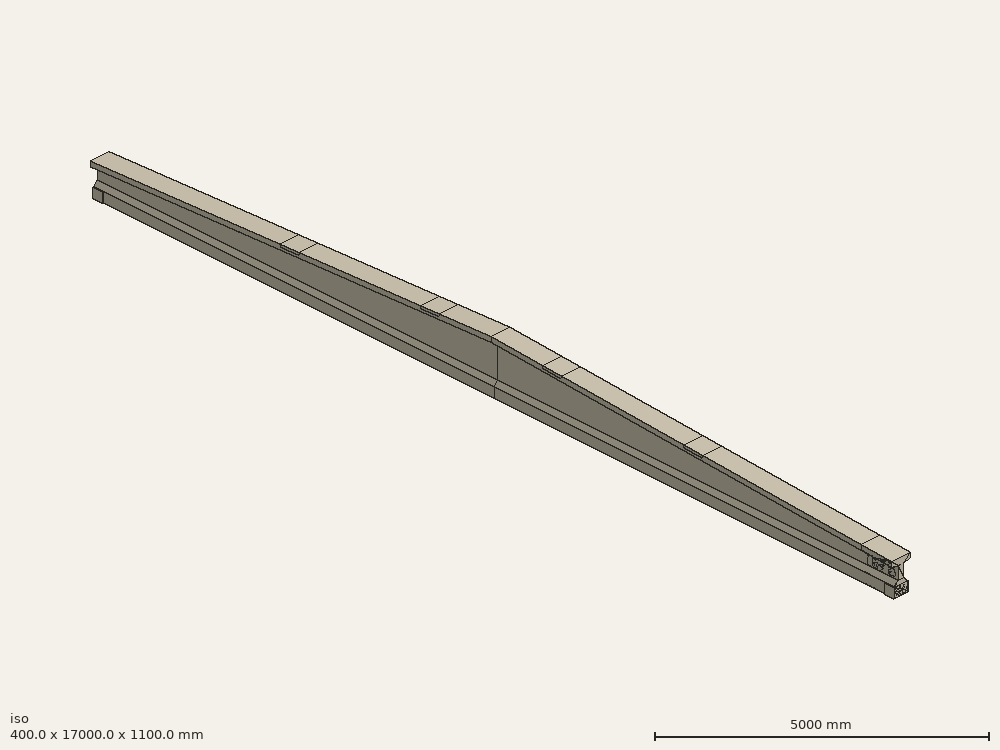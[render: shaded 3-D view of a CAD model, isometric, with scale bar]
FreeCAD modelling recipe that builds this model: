
FCSTD DOCUMENT  (FreeCAD 0.21R33694 (Git))
Label: beam_test
License: All rights reserved
LicenseURL: http://en.wikipedia.org/wiki/All_rights_reserved
objects: Fem::ConstraintForce×7, Sketcher::SketchObject×6, Part::FeaturePython×6, Part::Extrusion×3, Part::Feature×2, Fem::ConstraintDisplacement×2, Part::Loft×1, Part::Part2DObjectPython×1, App::DocumentObjectGroup×1, Part::Compound×1, Fem::FemSolverObjectPython×1, App::MaterialObjectPython×1, Fem::FeaturePython×1, Fem::FemMeshObjectPython×1, Fem::FemAnalysis×1
note: 20 computed .brp shape members not serialized (recipe doc carries the construction recipe); baked Part::Feature solids carry a one-line shape summary decoded from their .brp

FEATURE [Sketcher::SketchObject] Sketch
  FullyConstrained = true
  Placement = pos=(0,0,0) rot=(1,0,0;1.5708rad)
  sketch-geometry (12):
    g0: LineSegment StartX=-130 StartY=0 StartZ=0 EndX=130 EndY=4e-16 EndZ=0
    g1: LineSegment StartX=130 StartY=4e-16 StartZ=0 EndX=130 EndY=200 EndZ=0
    g2: LineSegment StartX=130 StartY=200 StartZ=0 EndX=60 EndY=290 EndZ=0
    g3: LineSegment StartX=60 StartY=290 StartZ=0 EndX=60 EndY=540 EndZ=0
    g4: LineSegment StartX=60 StartY=540 StartZ=0 EndX=200 EndY=570 EndZ=0
    g5: LineSegment StartX=200 StartY=570 StartZ=0 EndX=200 EndY=670 EndZ=0
    g6: LineSegment StartX=200 StartY=670 StartZ=0 EndX=-200 EndY=670 EndZ=0
    g7: LineSegment StartX=-200 StartY=670 StartZ=0 EndX=-200 EndY=570 EndZ=0
    g8: LineSegment StartX=-200 StartY=570 StartZ=0 EndX=-60 EndY=540 EndZ=0
    g9: LineSegment StartX=-60 StartY=540 StartZ=0 EndX=-60 EndY=290 EndZ=0
    g10: LineSegment StartX=-60 StartY=290 StartZ=0 EndX=-130 EndY=200 EndZ=0
    g11: LineSegment StartX=-130 StartY=200 StartZ=0 EndX=-130 EndY=0 EndZ=0
  constraints (33):
    c: PointOnObject(g0,g-1)
    c: Symmetric(g0,g0,g-2)
    c: DistanceX(g0,g0) = 260
    c: Coincident(g0,g1)
    c: Vertical(g1)
    c: Coincident(g1,g2)
    c: Coincident(g2,g3)
    c: Vertical(g3)
    c: Coincident(g3,g4)
    c: Coincident(g4,g5)
    c: Vertical(g5)
    c: Coincident(g5,g6)
    c: Coincident(g6,g7)
    c: Vertical(g7)
    c: Coincident(g7,g8)
    c: Coincident(g8,g9)
    c: Vertical(g9)
    c: Coincident(g9,g10)
    c: Coincident(g10,g11)
    c: Coincident(g11,g0)
    c: Vertical(g11)
    c: Equal(g11,g1)
    c: Symmetric(g9,g2,g-2)
    c: Equal(g9,g3)
    c: Symmetric(g6,g5,g-2)
    c: DistanceX(g6,g6) = 400
    c: DistanceY(g0,g5) = 670
    c: Equal(g7,g5)
    c: DistanceX(g9,g2) = 120
    c: DistanceY(g5,g5) = 100
    c: DistanceY(g3,g4) = 30
    c: DistanceY(g1,g1) = 200
    c: DistanceY(g1,g2) = 90
FEATURE [Sketcher::SketchObject] Sketch001
  FullyConstrained = true
  Placement = pos=(0,8500,0) rot=(1,0,0;1.5708rad)
  sketch-geometry (12):
    g0: LineSegment StartX=-130 StartY=0 StartZ=0 EndX=130 EndY=0 EndZ=0
    g1: LineSegment StartX=130 StartY=0 StartZ=0 EndX=130 EndY=200 EndZ=0
    g2: LineSegment StartX=130 StartY=200 StartZ=0 EndX=60 EndY=290 EndZ=0
    g3: LineSegment StartX=60 StartY=290 StartZ=0 EndX=60 EndY=970 EndZ=0
    g4: LineSegment StartX=60 StartY=970 StartZ=0 EndX=200 EndY=1000 EndZ=0
    g5: LineSegment StartX=200 StartY=1000 StartZ=0 EndX=200 EndY=1100 EndZ=0
    g6: LineSegment StartX=200 StartY=1100 StartZ=0 EndX=-200 EndY=1100 EndZ=0
    g7: LineSegment StartX=-200 StartY=1100 StartZ=0 EndX=-200 EndY=1000 EndZ=0
    g8: LineSegment StartX=-200 StartY=1000 StartZ=0 EndX=-60 EndY=970 EndZ=0
    g9: LineSegment StartX=-60 StartY=970 StartZ=0 EndX=-60 EndY=290 EndZ=0
    g10: LineSegment StartX=-60 StartY=290 StartZ=0 EndX=-130 EndY=200 EndZ=0
    g11: LineSegment StartX=-130 StartY=200 StartZ=0 EndX=-130 EndY=0 EndZ=0
  constraints (33):
    c: PointOnObject(g0,g-1)
    c: Symmetric(g0,g0,g-2)
    c: DistanceX(g0,g0) = 260
    c: Coincident(g0,g1)
    c: Vertical(g1)
    c: Coincident(g1,g2)
    c: Coincident(g2,g3)
    c: Vertical(g3)
    c: Coincident(g3,g4)
    c: Coincident(g4,g5)
    c: Vertical(g5)
    c: Coincident(g5,g6)
    c: Coincident(g6,g7)
    c: Vertical(g7)
    c: Coincident(g7,g8)
    c: Coincident(g8,g9)
    c: Vertical(g9)
    c: Coincident(g9,g10)
    c: Coincident(g10,g11)
    c: Coincident(g11,g0)
    c: Vertical(g11)
    c: Equal(g11,g1)
    c: Symmetric(g9,g2,g-2)
    c: Equal(g9,g3)
    c: Symmetric(g6,g5,g-2)
    c: DistanceX(g6,g6) = 400
    c: DistanceY(g0,g5) = 1100
    c: Equal(g7,g5)
    c: DistanceX(g9,g2) = 120
    c: DistanceY(g5,g5) = 100
    c: DistanceY(g3,g4) = 30
    c: DistanceY(g1,g1) = 200
    c: DistanceY(g1,g2) = 90
FEATURE [Part::Loft] Loft
  Closed = false
  MaxDegree = 5
  Ruled = false
  Sections = -> [Sketch,Sketch001]
  Solid = true
FEATURE [Part::Part2DObjectPython] Rectangle  # Draft 2D object (typed FeaturePython)
  Area = 3.16759e+06
  ChamferSize = 0
  Columns = 1
  FilletRadius = 0
  Height = 1690
  Length = 1874.31
  MakeFace = true
  Placement = pos=(-1011.48,650,-530.33) rot=(1,0,0;1.5708rad)
  Rows = 1
FEATURE [Part::Feature] Loft001
  Placement = pos=(1.041e-12,17000,0) rot=(0,0,1;3.14159rad)
  shape: bbox 400 x 8500 x 1100 mm, 14 faces (baked)
FEATURE [Part::Feature] Loft002
  shape: bbox 400 x 8500 x 1100 mm, 14 faces (baked)
FEATURE [Part::FeaturePython] Slice  # WARN: FeaturePython — macro-defined, semantics opaque (R4)
  Base = -> Loft002
  Mode = 1
  Tolerance = 0
  Tools = -> [Rectangle]
FEATURE [Part::FeaturePython] Slice_child0  label="Slice.0"  # WARN: FeaturePython — macro-defined, semantics opaque (R4)
  Base = -> Slice
  FilterType = 1
  Invert = false
  OverrideMaxVal = 0
  WindowFrom = 80
  WindowTo = 100
  items = 0
FEATURE [Part::FeaturePython] Slice_child1  label="Slice.1"  # WARN: FeaturePython — macro-defined, semantics opaque (R4)
  Base = -> Slice
  FilterType = 1
  Invert = false
  OverrideMaxVal = 0
  WindowFrom = 80
  WindowTo = 100
  items = 1
FEATURE [App::DocumentObjectGroup] GrExplode_Slice  label="Exploded Slice"
  Group = -> [Slice_child0,Slice_child1]
FEATURE [Part::FeaturePython] Facebinder  # WARN: FeaturePython — macro-defined, semantics opaque (R4)
  Area = 150846
  Extrusion = 0
  Faces = -> [Slice_child1]
  RemoveSplitter = false
  Sew = false
FEATURE [Sketcher::SketchObject] Sketch002  label="Lage_Spannkabel"
  FullyConstrained = false
  MapMode = 5
  Placement = pos=(0,650,0) rot=(1,0,0;1.5708rad)
  Support = -> [Facebinder]
  sketch-geometry (2):
    g0: LineSegment StartX=0 StartY=0 StartZ=0 EndX=0 EndY=362 EndZ=0
    g1: LineSegment StartX=0 StartY=100 StartZ=0 EndX=947.371 EndY=100 EndZ=0
  constraints (6):
    c: Coincident(g0,g-1)
    c: Vertical(g0)
    c: DistanceY(g0,g0) = 362
    c: PointOnObject(g1,g0)
    c: Horizontal(g1)
    c: DistanceY(g1,g0) = 262
FEATURE [Sketcher::SketchObject] Sketch003
  ExternalGeometry = -> [Sketch002]
  FullyConstrained = true
  MapMode = 5
  Placement = pos=(0,0,0) rot=(1,0,0;1.5708rad)
  Support = -> [Loft]
  sketch-geometry (4):
    g0: LineSegment StartX=-150 StartY=200 StartZ=0 EndX=150 EndY=200 EndZ=0
    g1: LineSegment StartX=150 StartY=200 StartZ=0 EndX=150 EndY=0 EndZ=0
    g2: LineSegment StartX=150 StartY=0 StartZ=0 EndX=-150 EndY=0 EndZ=0
    g3: LineSegment StartX=-150 StartY=0 StartZ=0 EndX=-150 EndY=200 EndZ=0
  constraints (10):
    c: Coincident(g0,g1)
    c: Coincident(g1,g2)
    c: Coincident(g2,g3)
    c: Coincident(g3,g0)
    c: Horizontal(g0)
    c: Vertical(g3)
    c: Symmetric(g1,g0,g-3)
    c: Symmetric(g2,g1,g-2)
    c: DistanceX(g2,g2) = 300
    c: PointOnObject(g1,g-1)
FEATURE [Part::Extrusion] Extrude  label="Lager_links"
  Base = -> Sketch003
  Dir = (0,1,0)
  DirMode = 0
  FaceMakerClass = Part::FaceMakerBullseye
  LengthFwd = 200
  LengthRev = 0
  Solid = true
  Symmetric = false
FEATURE [Part::FeaturePython] Clone  label="Lager_rechts"  # Draft clone (typed FeaturePython)
  AttacherType = Attacher::AttachEngine3D
  Fuse = false
  Objects = -> [Extrude]
  Placement = pos=(1.0409e-12,16800,2e-16) rot=(0,0,1;0rad)
  Scale = (1,1,1)
FEATURE [Sketcher::SketchObject] Sketch004
  ExternalGeometry = -> [Loft]
  FullyConstrained = true
  MapMode = 5
  Placement = pos=(0,-33.8076,668.29) rot=(1,0,0;0.050545rad)
  Support = -> [Loft]
  sketch-geometry (12):
    g0: LineSegment StartX=-200 StartY=7444.72 StartZ=0 EndX=200 EndY=7444.72 EndZ=0
    g1: LineSegment StartX=200 StartY=7444.72 StartZ=0 EndX=200 EndY=7044.72 EndZ=0
    g2: LineSegment StartX=200 StartY=7044.72 StartZ=0 EndX=-200 EndY=7044.72 EndZ=0
    g3: LineSegment StartX=-200 StartY=7044.72 StartZ=0 EndX=-200 EndY=7444.72 EndZ=0
    g4: LineSegment StartX=-200 StartY=4444.72 StartZ=0 EndX=200 EndY=4444.72 EndZ=0
    g5: LineSegment StartX=200 StartY=4444.72 StartZ=0 EndX=200 EndY=4044.72 EndZ=0
    g6: LineSegment StartX=200 StartY=4044.72 StartZ=0 EndX=-200 EndY=4044.72 EndZ=0
    g7: LineSegment StartX=-200 StartY=4044.72 StartZ=0 EndX=-200 EndY=4444.72 EndZ=0
    g8: LineSegment StartX=-200 StartY=7044.72 StartZ=0 EndX=0 EndY=7244.72 EndZ=0
    g9: LineSegment StartX=0 StartY=7244.72 StartZ=0 EndX=200 EndY=7444.72 EndZ=0
    g10: LineSegment StartX=-200 StartY=4044.72 StartZ=0 EndX=0 EndY=4244.72 EndZ=0
    g11: LineSegment StartX=0 StartY=4244.72 StartZ=0 EndX=200 EndY=4444.72 EndZ=0
  constraints (32):
    c: Coincident(g0,g1)
    c: Coincident(g1,g2)
    c: Coincident(g2,g3)
    c: Coincident(g3,g0)
    c: Horizontal(g0)
    c: Vertical(g1)
    c: Vertical(g3)
    c: Coincident(g4,g5)
    c: Coincident(g5,g6)
    c: Coincident(g6,g7)
    c: Coincident(g7,g4)
    c: Horizontal(g4)
    c: Vertical(g5)
    c: Vertical(g7)
    c: Symmetric(g2,g1,g-2)
    c: DistanceX(g2,g2) = 400
    c: Symmetric(g6,g5,g-2)
    c: Equal(g2,g6)
    c: Coincident(g2,g8)
    c: PointOnObject(g8,g-2)
    c: Coincident(g8,g9)
    c: Coincident(g9,g0)
    c: Coincident(g6,g10)
    c: PointOnObject(g10,g-2)
    c: Coincident(g11,g10)
    c: Coincident(g11,g4)
    c: Parallel(g10,g11)
    c: Equal(g6,g5)
    c: Parallel(g8,g9)
    c: Equal(g2,g1)
    c: DistanceY(g8,g-3) = 1300
    c: DistanceY(g10,g8) = 3000
FEATURE [Part::Extrusion] Extrude001  label="Auflager_Mast"
  Base = -> Sketch004
  Dir = (0,-0.0505236,0.998723)
  DirMode = 2
  FaceMakerClass = Part::FaceMakerBullseye
  LengthFwd = 50
  LengthRev = 0
  Reversed = true
  Solid = true
  Symmetric = false
FEATURE [Sketcher::SketchObject] Sketch005
  ExternalGeometry = -> [Extrude001,Loft001]
  FullyConstrained = true
  MapMode = 5
  Placement = pos=(1.041e-12,17033.8,668.29) rot=(0,0.02527,0.999681;3.14159rad)
  Support = -> [Loft001]
  sketch-geometry (8):
    g0: LineSegment StartX=-200 StartY=7450.34 StartZ=0 EndX=200 EndY=7450.34 EndZ=0
    g1: LineSegment StartX=200 StartY=7450.34 StartZ=0 EndX=200 EndY=7050.34 EndZ=0
    g2: LineSegment StartX=200 StartY=7050.34 StartZ=0 EndX=-200 EndY=7050.34 EndZ=0
    g3: LineSegment StartX=-200 StartY=7050.34 StartZ=0 EndX=-200 EndY=7450.34 EndZ=0
    g4: LineSegment StartX=-200 StartY=4465.65 StartZ=0 EndX=200 EndY=4465.65 EndZ=0
    g5: LineSegment StartX=200 StartY=4465.65 StartZ=0 EndX=200 EndY=4065.65 EndZ=0
    g6: LineSegment StartX=200 StartY=4065.65 StartZ=0 EndX=-200 EndY=4065.65 EndZ=0
    g7: LineSegment StartX=-200 StartY=4065.65 StartZ=0 EndX=-200 EndY=4465.65 EndZ=0
  constraints (22):
    c: Coincident(g0,g1)
    c: Coincident(g1,g2)
    c: Coincident(g2,g3)
    c: Coincident(g3,g0)
    c: Horizontal(g0)
    c: Horizontal(g2)
    c: Vertical(g1)
    c: Vertical(g3)
    c: Coincident(g4,g5)
    c: Coincident(g5,g6)
    c: Coincident(g6,g7)
    c: Coincident(g7,g4)
    c: Horizontal(g4)
    c: Horizontal(g6)
    c: Vertical(g5)
    c: Vertical(g7)
    c: Symmetric(g0,g-3,g-5)
    c: Vertical(g0,g-5)
    c: Vertical(g-5,g4)
    c: Symmetric(g4,g-4,g-5)
    c: Equal(g6,g7)
    c: Equal(g7,g3)
FEATURE [Part::Extrusion] Extrude002  label="Auflager_dummy"
  Base = -> Sketch005
  Dir = (0,0.0505236,0.998723)
  DirMode = 2
  FaceMakerClass = Part::FaceMakerBullseye
  LengthFwd = 50
  LengthRev = 0
  Reversed = true
  Solid = true
  Symmetric = false
FEATURE [Part::FeaturePython] BooleanFragments  # WARN: FeaturePython — macro-defined, semantics opaque (R4)
  Mode = 2
  Objects = -> [Loft,Loft001,Extrude,Clone,Extrude001,Extrude002]
  Tolerance = 0
FEATURE [Part::Compound] Compound
  Links = -> [BooleanFragments]
FEATURE [Fem::FemSolverObjectPython] SolverCcxTools  # FEM object (typed FeaturePython)
  AnalysisType = 0
  BeamShellResultOutput3D = true
  BucklingFactors = 1
  EigenmodeHighLimit = 1000000
  EigenmodeLowLimit = 0
  EigenmodesCount = 10
  GeometricalNonlinearity = 0
  IterationsControlParameterCutb = 0.25,0.5,0.75,0.85,,,1.5,
  IterationsControlParameterIter = 4,8,9,200,10,400,,200,,
  IterationsControlParameterTimeUse = false
  IterationsThermoMechMaximum = 2000
  IterationsUserDefinedIncrementations = false
  IterationsUserDefinedTimeStepLength = false
  MaterialNonlinearity = 0
  MatrixSolverType = 0
  SplitInputWriter = true
  ThermoMechSteadyState = true
  TimeEnd = 1
  TimeInitialStep = 0.01
FEATURE [App::MaterialObjectPython] MaterialSolid  label="B450"  # material (typed FeaturePython)
  Category = 0
  Material = AngleOfFriction=30 deg,AuthorAndLicense=(c) 2019 Bernd Hahnebach (CC-BY 3.0),CardName=Concrete-EN-C35_45,CompressiveStrength=15.75 MPa,+7 more (map truncated)
FEATURE [Fem::ConstraintDisplacement] ConstraintDisplacement  label="XYZ"
  NormalDirection = (0,0,-1)
  Normals = (4) [(0,0,-1),(0,0,-1),(0,0,-1),(0,0,-1)]
  Points = (4) [(-130,0,0),(-43.3333,0,0),(43.3333,0,0),(130,0,0)]
  References = -> [Compound]
  Scale = 17
  hasXFormula = false
  hasYFormula = false
  hasZFormula = false
  rotxFix = false
  rotxFree = true
  rotyFix = false
  rotyFree = true
  rotzFix = false
  rotzFree = true
  useFlowSurfaceForce = false
  xDisplacement = 0
  xFix = true
  xFree = false
  xRotation = 0
  yDisplacement = 0
  yFix = true
  yFree = false
  yRotation = 0
  zDisplacement = 0
  zFix = true
  zFree = false
  zRotation = 0
FEATURE [Fem::ConstraintDisplacement] ConstraintDisplacement001  label="XZ"
  NormalDirection = (0,0,-1)
  Normals = (4) [(0,0,-1),(0,0,-1),(0,0,-1),(0,0,-1)]
  Points = (4) [(130,17000,0),(43.3333,17000,0),(-43.3333,17000,0),(-130,17000,0)]
  References = -> [Compound]
  Scale = 17
  hasXFormula = false
  hasYFormula = false
  hasZFormula = false
  rotxFix = false
  rotxFree = true
  rotyFix = false
  rotyFree = true
  rotzFix = false
  rotzFree = true
  useFlowSurfaceForce = false
  xDisplacement = 0
  xFix = true
  xFree = false
  xRotation = 0
  yDisplacement = 0
  yFix = false
  yFree = true
  yRotation = 0
  zDisplacement = 0
  zFix = true
  zFree = false
  zRotation = 0
FEATURE [Fem::FeaturePython] MeshRegion  # FEM object (typed FeaturePython)
  CharacteristicLength = 1000
  References = -> [Compound]
FEATURE [Fem::FemMeshObjectPython] FEMMeshGmsh  # FEM object (typed FeaturePython)
  Algorithm2D = 0
  Algorithm3D = 0
  CharacteristicLengthMax = 1000
  CharacteristicLengthMin = 0
  CoherenceMesh = true
  ElementDimension = 3
  ElementOrder = 1
  GeometryTolerance = 1e-06
  GroupsOfNodes = false
  HighOrderOptimize = 0
  MeshRegionList = -> [MeshRegion]
  MeshSizeFromCurvature = 12
  OptimizeNetgen = false
  OptimizeStd = true
  Part = -> Compound
  RecombinationAlgorithm = 0
  Recombine3DAll = false
  RecombineAll = false
  SecondOrderLinear = false
FEATURE [Fem::ConstraintForce] ConstraintForce004  label="Mast_vertikal"
  Direction = -> Compound [Edge31]
  DirectionVector = (0,0,-1)
  Force = 18000
  NormalDirection = (0,-0.0505236,0.998723)
  Points = (16) [(200,7001.92,1024.21),(66.6667,7001.92,1024.21),(-66.6667,7001.92,1024.21),(-200,7001.92,1024.21),(200,7135.08,1030.95),(66.6667,7135.08,1030.95),+10 more]
  References = -> [Compound]
  Reversed = true
  Scale = 22
FEATURE [Fem::ConstraintForce] ConstraintForce005  label="Rahmen"
  Direction = -> Compound [Edge31]
  DirectionVector = (0,0,-1)
  Force = 2400
  NormalDirection = (0,-0.0505236,0.998723)
  Points = (16) [(200,4005.75,872.644),(66.6667,4005.75,872.644),(-66.6667,4005.75,872.644),(-200,4005.75,872.644),(200,4138.91,879.38),(66.6667,4138.91,879.38),+10 more]
  References = -> [Compound]
  Reversed = true
  Scale = 22
FEATURE [Fem::ConstraintForce] ConstraintForce  label="prestress1(p)"
  Direction = -> Compound [Edge164]
  DirectionVector = (0,-1,0)
  Force = 900000
  NormalDirection = (0,1,-2e-16)
  Points = (4) [(-26.4133,17000,32.3139),(-69.7586,17000,120.318),(69.7586,17000,79.6821),(26.4133,17000,167.686)]
  References = -> [Compound]
  Reversed = true
  Scale = 19
FEATURE [Fem::ConstraintForce] ConstraintForce006  label="prestress2(p)"
  DirectionVector = (0,1,-2e-16)
  Force = 900000
  NormalDirection = (0,-1,2e-16)
  Points = (4) [(26.4133,7.10905e-15,32.3139),(69.7586,2.64699e-14,120.318),(-69.7586,1.75301e-14,79.6821),(-26.4133,3.6891e-14,167.686)]
  References = -> [Compound]
  Reversed = true
  Scale = 19
FEATURE [Fem::ConstraintForce] ConstraintForce007  label="Roof_weight"
  Direction = -> Compound [Edge33]
  DirectionVector = (0,0,-1)
  Force = 214000
  NormalDirection = (0,-0.0505236,0.998723)
  Points = (248) [(200,0,670),(66.6667,0,670),(-66.6667,0,670),(-200,0,670),(200,445.083,692.516),(66.6667,445.083,692.516),(-66.6667,445.083,692.516),+241 more]
  References = -> [Compound]
  Reversed = true
  Scale = 46
FEATURE [Fem::ConstraintForce] ConstraintForce008  label="V(p)"
  DirectionVector = (0,0,1)
  Force = 73476
  NormalDirection = (0,0,-1)
  Points = (32) [(-130,0,0),(-43.3333,0,0),(43.3333,0,0),(130,0,0),(-130,66.6667,0),(-43.3333,66.6667,0),(43.3333,66.6667,0),(130,66.6667,0),(-130,133.333,0),+23 more]
  References = -> [Compound]
  Reversed = true
  Scale = 16
FEATURE [Fem::ConstraintForce] ConstraintForce009  label="V(v)"
  DirectionVector = (0,0,1)
  Force = 234398
  NormalDirection = (0,0,-1)
  Points = (32) [(130,17000,0),(43.3333,17000,0),(-43.3333,17000,0),(-130,17000,0),(130,16933.3,0),(43.3333,16933.3,0),(-43.3333,16933.3,0),(-130,16933.3,0),+24 more]
  References = -> [Compound]
  Reversed = true
  Scale = 16
FEATURE [Fem::FemAnalysis] Analysis
  Group = -> [SolverCcxTools,MaterialSolid,ConstraintDisplacement,ConstraintDisplacement001,FEMMeshGmsh,ConstraintForce004,ConstraintForce005,ConstraintForce,ConstraintForce006,ConstraintForce007,ConstraintForce008,ConstraintForce009]
